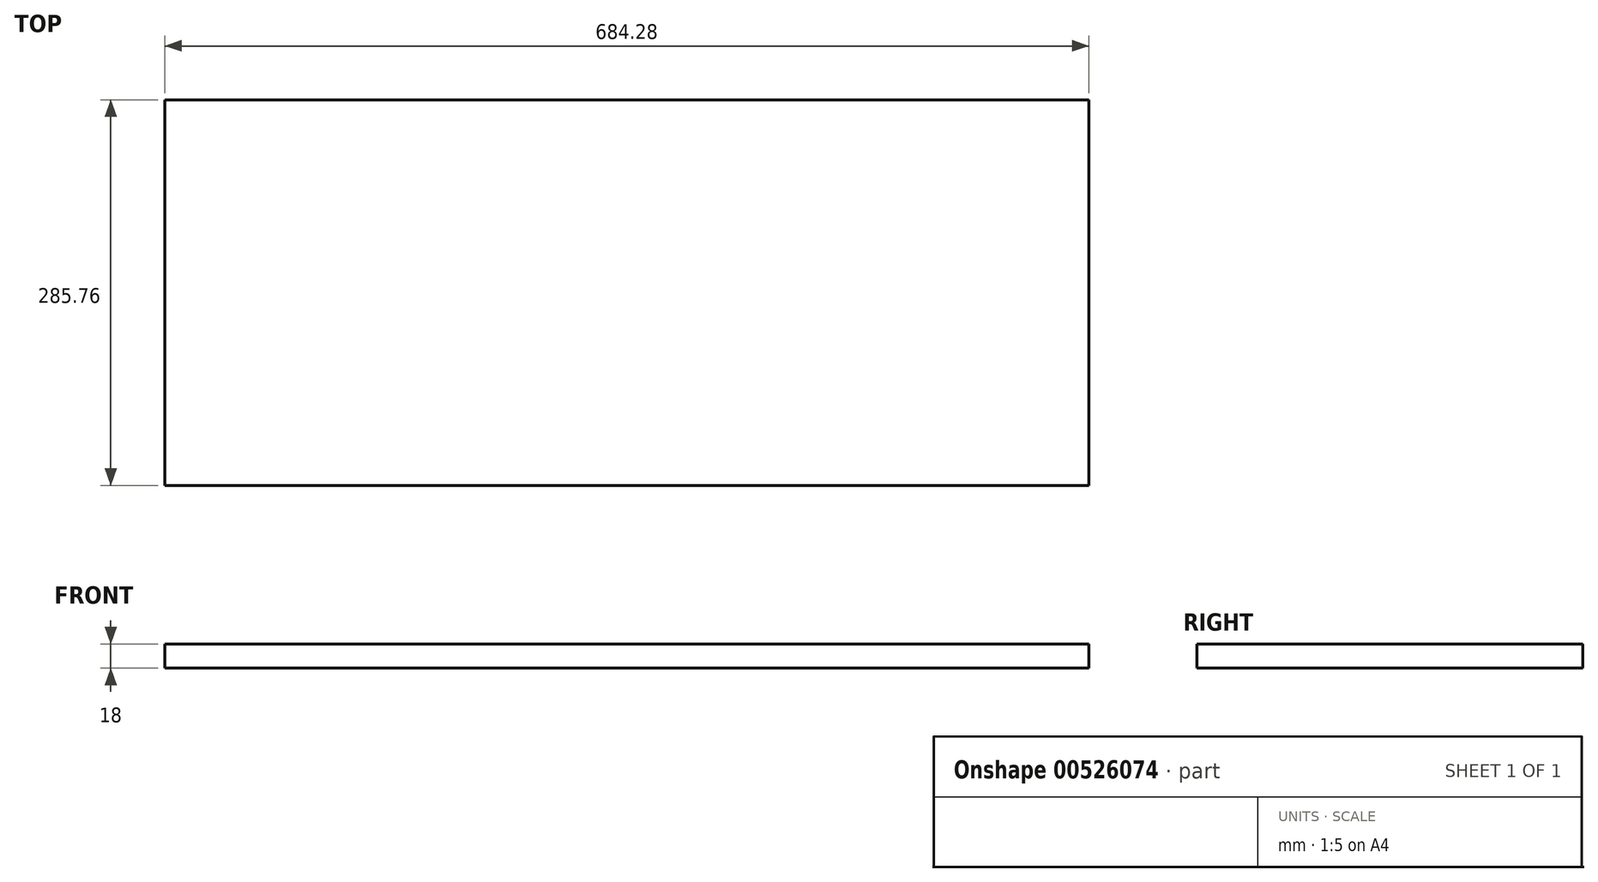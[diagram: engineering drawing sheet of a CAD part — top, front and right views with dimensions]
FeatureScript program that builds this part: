
annotation { "Feature Type Name" : "Feature", "Feature Type Description" : "" }
export const myFeature = defineFeature(function(context is Context, id is Id, definition is map)
    precondition{}
    {
        {
            var Q0;
            Q0=qCreatedBy(makeId("Top.planeOp"),FACE);
            var sketch = newSketch(context, id + "F0", { "sketchPlane" : qUnion([Q0])});
            skLineSegment(sketch, "E0.rect.bottom", {"start": v(342.14, -142.87) * mm, "end": v(-342.14, -142.88) * mm});
            skPoint(sketch, "E0.rect.middle", {"position": v(0, 0) * mm});
            skLineSegment(sketch, "E1", {"start": v(-318.66, 142.88) * mm, "end": v(342.14, 142.88) * mm});
            skLineSegment(sketch, "E2", {"start": v(-342.14, -142.88) * mm, "end": v(-342.14, 142.88) * mm});
            skLineSegment(sketch, "E3", {"start": v(-342.14, 142.88) * mm, "end": v(-318.66, 142.88) * mm});
            skLineSegment(sketch, "E4", {"start": v(342.14, 142.88) * mm, "end": v(342.14, -142.87) * mm});
            skSolve(sketch);
        }
        {
            var Q0;
            Q0=makeQuery(id+"F0.imprint","IMPRINT",FACE,{"disambiguationData":[TD([[makeQuery(id+"F0.imprint","IMPRINT",EDGE,{"derivedFrom":sQuery(id+"F0.wireOp",EDGE,"E0.rect.bottom")}),-1.0]])]});
            extrude(context, id + "F1", {"entities" : qUnion([Q0]), "depth" : 18 * mm, "offsetDistance" : 30.48 * mm});
        }
    });
